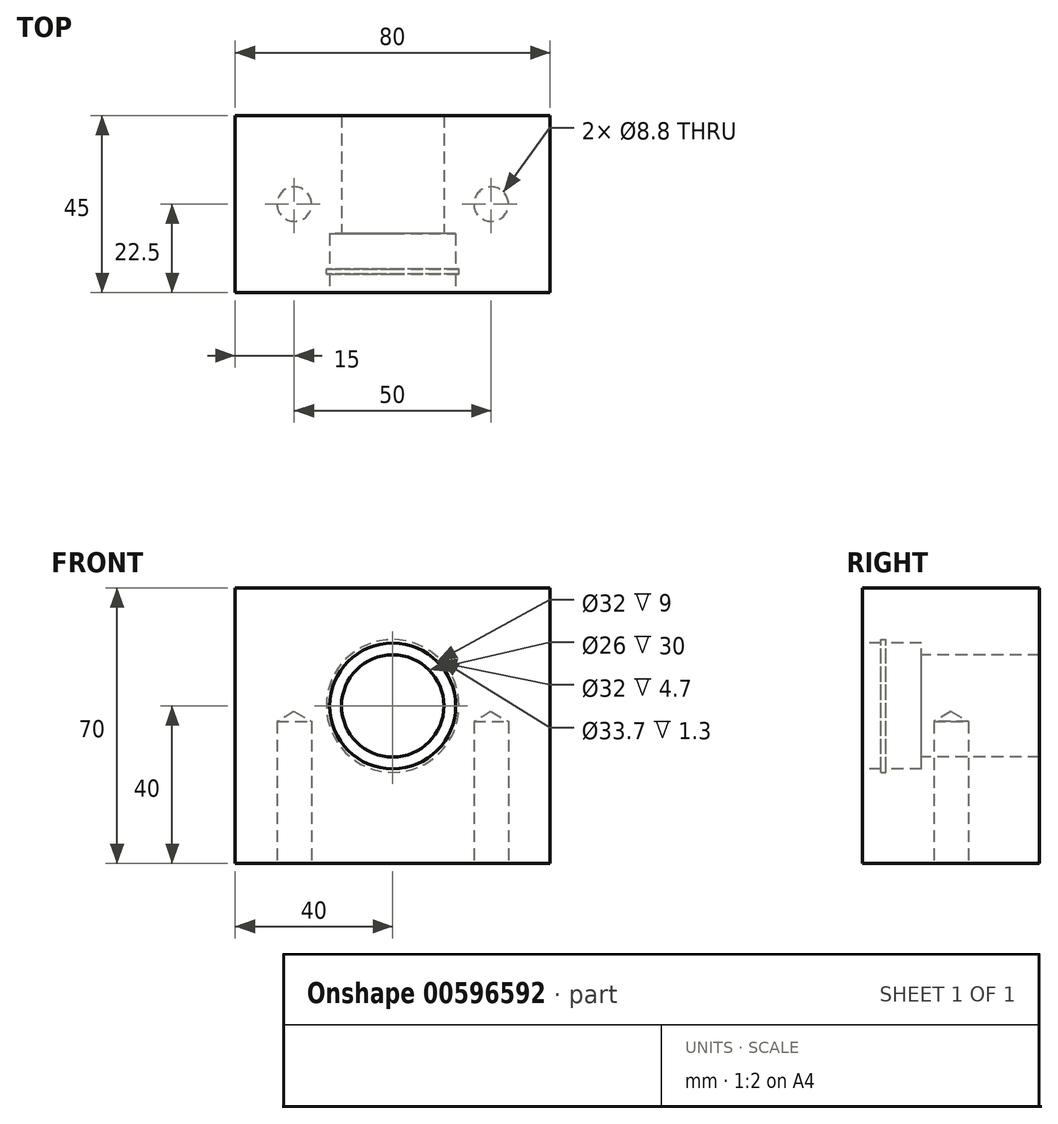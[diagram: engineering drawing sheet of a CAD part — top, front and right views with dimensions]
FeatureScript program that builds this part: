
annotation { "Feature Type Name" : "Feature", "Feature Type Description" : "" }
export const myFeature = defineFeature(function(context is Context, id is Id, definition is map)
    precondition{}
    {
        {
            var Q0;
            Q0=qCreatedBy(makeId("Front.planeOp"),FACE);
            var sketch = newSketch(context, id + "F0", { "sketchPlane" : qUnion([Q0])});
            skLineSegment(sketch, "E0.bottom", {"start": v(0, 0) * mm, "end": v(80, 0) * mm});
            skLineSegment(sketch, "E0.top", {"start": v(0, 70) * mm, "end": v(80, 70) * mm});
            skLineSegment(sketch, "E0.left", {"start": v(0, 0) * mm, "end": v(0, 70) * mm});
            skLineSegment(sketch, "E0.right", {"start": v(80, 0) * mm, "end": v(80, 70) * mm});
            skSolve(sketch);
        }
        {
            var Q0;
            Q0 = qSketchRegion(id + "F0", true);
            extrude(context, id + "F1", {"entities" : qUnion([Q0]), "depth" : 45 * mm, "offsetDistance" : 25 * mm});
        }
        {
            var Q0;
            Q0=makeQuery(id+"F1.opExtrude","CAP_FACE",FACE,{"disambiguationData":[OSD([sQuery(id+"F0.wireOp",EDGE,"E0.bottom"),sQuery(id+"F0.wireOp",EDGE,"E0.top"),sQuery(id+"F0.wireOp",EDGE,"E0.left"),sQuery(id+"F0.wireOp",EDGE,"E0.right")])],"isStart":false});
            var sketch = newSketch(context, id + "F2", { "sketchPlane" : qUnion([Q0])});
            skCircle(sketch, "E1", {"center": v(40, 40) * mm, "radius": 13 * mm});
            skPoint(sketch, "E1.centerSnap0", {"position": v(40, 70) * mm});
            skSolve(sketch);
        }
        {
            var Q0;
            Q0=makeQuery(id+"F2.imprint","IMPRINT",FACE,{"disambiguationData":[TD([[makeQuery(id+"F2.imprint","IMPRINT",EDGE,{"derivedFrom":sQuery(id+"F2.wireOp",EDGE,"E1")}),1.0]])]});
            extrude(context, id + "F3", {"entities" : qUnion([Q0]), "operationType" : NewBodyOperationType.REMOVE, "endBound" : BoundingType.THROUGH_ALL, "oppositeDirection" : true, "depth" : 25 * mm, "offsetDistance" : 25 * mm});
        }
        {
            var Q0;
            Q0=makeQuery(id+"F1.opExtrude","CAP_FACE",FACE,{"disambiguationData":[OSD([sQuery(id+"F0.wireOp",EDGE,"E0.bottom"),sQuery(id+"F0.wireOp",EDGE,"E0.top"),sQuery(id+"F0.wireOp",EDGE,"E0.left"),sQuery(id+"F0.wireOp",EDGE,"E0.right")])],"isStart":false});
            var sketch = newSketch(context, id + "F4", { "sketchPlane" : qUnion([Q0])});
            skCircle(sketch, "E2", {"center": v(40, 40) * mm, "radius": 16 * mm});
            skSolve(sketch);
        }
        {
            var Q0;
            Q0=makeQuery(id+"F4.imprint","IMPRINT",FACE,{"disambiguationData":[TD([[makeQuery(id+"F4.imprint","IMPRINT",EDGE,{"derivedFrom":sQuery(id+"F4.wireOp",EDGE,"E2")}),1.0]])]});
            extrude(context, id + "F5", {"entities" : qUnion([Q0]), "operationType" : NewBodyOperationType.REMOVE, "oppositeDirection" : true, "depth" : 15 * mm, "offsetDistance" : 25 * mm});
        }
        {
            var Q0;
            Q0=makeQuery(id+"F5.boolean.opBoolean","COPY",FACE,{"derivedFrom":makeQuery(id+"F5.opExtrude","CAP_FACE",FACE,{"disambiguationData":[OSD([sQuery(id+"F2.wireOp",EDGE,"E1"),sQuery(id+"F4.wireOp",EDGE,"E2")])],"isStart":false})});
            cPlane(context, id + "F6", {"entities" : qUnion([Q0]), "cplaneType" : CPlaneType.OFFSET, "offset" : 9 * mm, "width" : 150 * mm, "height" : 150 * mm});
        }
        {
            var Q0;
            Q0=qCreatedBy(id+"F6.planeOp",FACE);
            var sketch = newSketch(context, id + "F7", { "sketchPlane" : qUnion([Q0])});
            skCircle(sketch, "E3", {"center": v(40, 40) * mm, "radius": 16.85 * mm});
            skSolve(sketch);
        }
        {
            var Q0;
            Q0=makeQuery(id+"F7.imprint","IMPRINT",FACE,{"disambiguationData":[TD([[makeQuery(id+"F7.imprint","IMPRINT",EDGE,{"derivedFrom":sQuery(id+"F7.wireOp",EDGE,"E3")}),1.0]])]});
            extrude(context, id + "F8", {"entities" : qUnion([Q0]), "operationType" : NewBodyOperationType.REMOVE, "depth" : 1.3 * mm, "offsetDistance" : 25 * mm});
        }
        {
            var Q0;
            Q0=makeQuery(id+"F1.opExtrude","SWEPT_FACE",FACE,{"disambiguationData":[OSD([sQuery(id+"F0.wireOp",EDGE,"E0.bottom")])]});
            var sketch = newSketch(context, id + "F9", { "sketchPlane" : qUnion([Q0])});
            skPoint(sketch, "E4", {"position": v(15, 22.5) * mm});
            skPoint(sketch, "E4.positionSnap0", {"position": v(0, 22.5) * mm});
            skPoint(sketch, "E5", {"position": v(65, 22.5) * mm});
            skSolve(sketch);
        }
        {
            var Q0;
            Q0=sQuery(id+"F9.wireOp",VERTEX,"E4");
            var Q1;
            Q1=sQuery(id+"F9.wireOp",VERTEX,"E5");
            var Q2;
            Q2=makeQuery(id+"F1.opExtrude","SWEPT_BODY",BODY,{"disambiguationData":[OSD([sQuery(id+"F0.wireOp",EDGE,"E0.bottom"),sQuery(id+"F0.wireOp",EDGE,"E0.top"),sQuery(id+"F0.wireOp",EDGE,"E0.left"),sQuery(id+"F0.wireOp",EDGE,"E0.right")])]});
            hole(context, id + "F10", {"style" : HoleStyle.SIMPLE, "endStyle" : HoleEndStyle.BLIND, "standardTappedOrClearance" : lookupTablePath({ "standard" : "ISO", "fit" : "Normal", "size" : "M8", "type" : "Clearance" }), "standardBlindInLast" : lookupTablePath({ "fit" : "Standard", "standard" : "ISO", "size" : "M8", "type" : "Clearance" }), "holeDiameter" : 8.8 * mm, "majorDiameter" : 5 * mm, "holeDepth" : 36 * mm, "isTappedThrough" : true, "tappedDepth" : 12 * mm, "tapClearance" : 3, "startFromSketch" : true, "locations" : qUnion([Q0, Q1]), "scope" : qUnion([Q2])});
        }
    });
